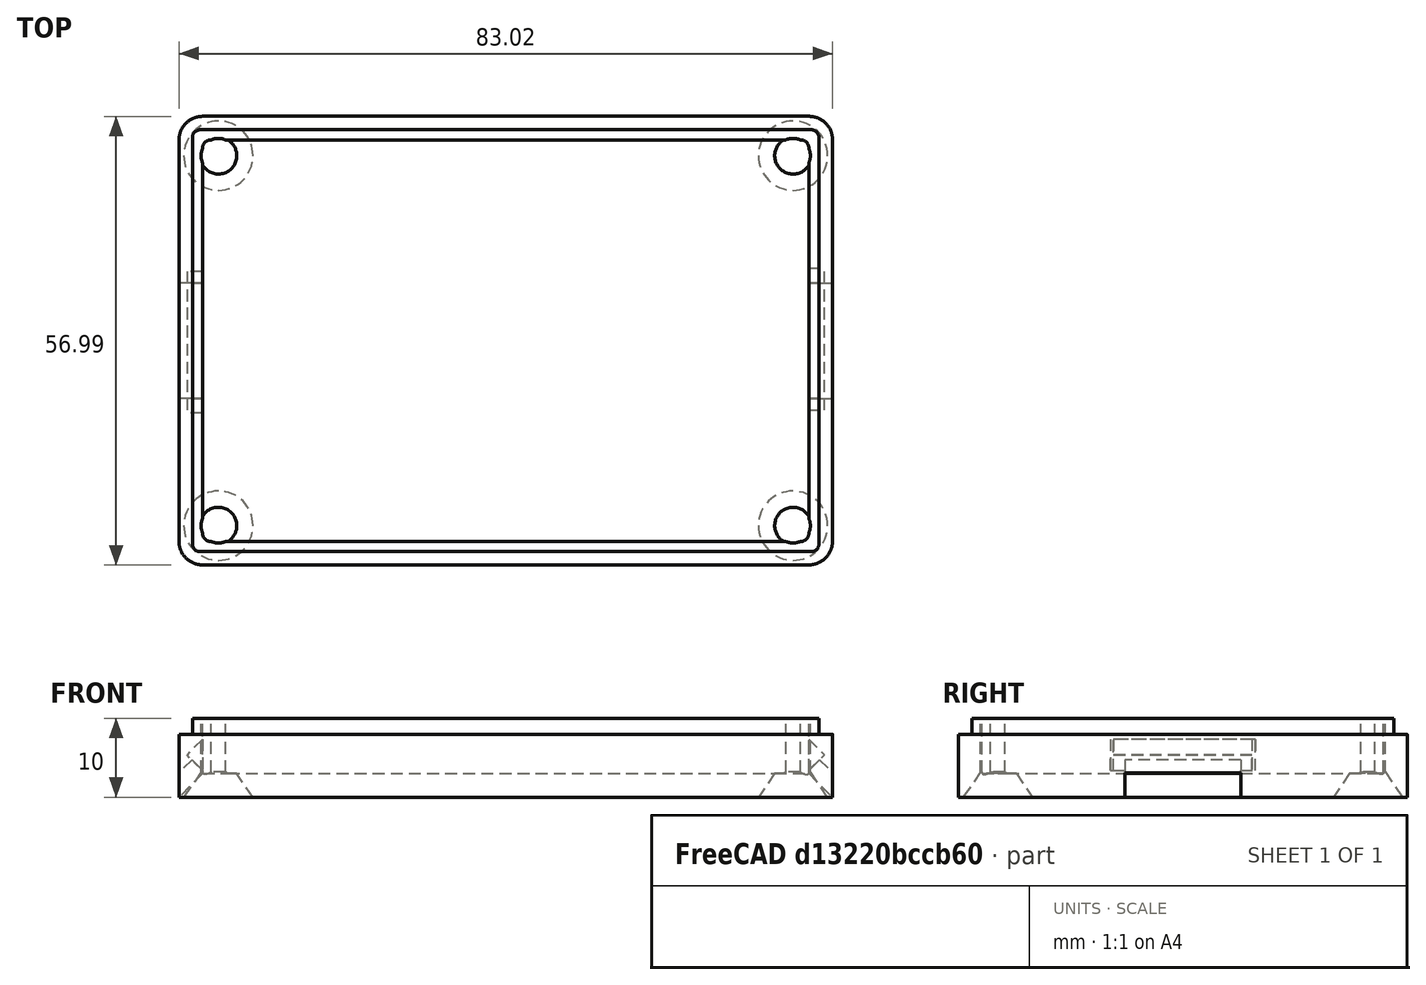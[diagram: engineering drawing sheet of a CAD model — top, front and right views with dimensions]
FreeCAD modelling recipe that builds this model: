
FCSTD DOCUMENT  (FreeCAD 0.18.4R)
Label: MidBoxBottom
License: All rights reserved
LicenseURL: http://en.wikipedia.org/wiki/All_rights_reserved
objects: Part::Box×11, Part::MultiFuse×8, Part::Cut×5, Part::Cylinder×4, Part::Cone×4, Part::Fillet×2, Sketcher::SketchObject×1, PartDesign::Pad×1, Mesh::Feature×1
note: 37 computed .brp shape members not serialized (recipe doc carries the construction recipe); baked Part::Feature solids carry a one-line shape summary decoded from their .brp

FEATURE [Sketcher::SketchObject] Sketch002
  MapMode = 5
  sketch-geometry (8):
    g0: LineSegment StartX=6.98534 StartY=-27.9862 StartZ=0 EndX=-70.0102 EndY=-27.9862 EndZ=0
    g1: LineSegment StartX=-73.0017 StartY=-24.9946 StartZ=0 EndX=-73.0017 EndY=25.9928 EndZ=0
    g2: LineSegment StartX=-69.9918 StartY=29.0027 StartZ=0 EndX=7.02245 EndY=29.0027 EndZ=0
    g3: LineSegment StartX=10.0166 StartY=26.0085 StartZ=0 EndX=10.0166 EndY=-24.9549 EndZ=0
    g4: ArcOfCircle CenterX=6.98534 CenterY=-24.9549 CenterZ=0 NormalX=0 NormalY=0 NormalZ=1 AngleXU=0 Radius=3.0313 StartAngle=4.71239 EndAngle=6.28319
    g5: ArcOfCircle CenterX=-70.0102 CenterY=-24.9946 CenterZ=0 NormalX=0 NormalY=0 NormalZ=1 AngleXU=0 Radius=2.99151 StartAngle=3.14159 EndAngle=4.71239
    g6: ArcOfCircle CenterX=-69.9918 CenterY=25.9928 CenterZ=0 NormalX=0 NormalY=0 NormalZ=1 AngleXU=0 Radius=3.00989 StartAngle=1.5708 EndAngle=3.14159
    g7: ArcOfCircle CenterX=7.02245 CenterY=26.0085 CenterZ=0 NormalX=0 NormalY=0 NormalZ=1 AngleXU=0 Radius=2.99419 StartAngle=1.03e-13 EndAngle=1.5708
  constraints (12):
    c: Horizontal(g0)
    c: Horizontal(g2)
    c: Vertical(g1)
    c: Vertical(g3)
    c: Tangent(g3,g4) = 1.5708
    c: Tangent(g0,g4) = 1.5708
    c: Tangent(g1,g5) = 1.5708
    c: Tangent(g0,g5) = 1.5708
    c: Tangent(g1,g6) = 1.5708
    c: Tangent(g2,g6) = 1.5708
    c: Tangent(g2,g7) = 1.5708
    c: Tangent(g3,g7) = 1.5708
FEATURE [PartDesign::Pad] Pad013
  Length = 10
  Length2 = 100
  Profile = -> Sketch002
  Type = 0
FEATURE [Part::Box] Box010  label="Würfel010"
  AttacherType = Attacher::AttachEngine3D
  Height = 9
  Length = 77
  Placement = pos=(-70,-25,3) rot=(0,0,1;0rad)
  Width = 51
FEATURE [Part::Cut] Cut011  label="Box raw"
  Base = -> Pad013
  Tool = -> Box010
FEATURE [Part::Box] Box  label="Rand002"
  AttacherType = Attacher::AttachEngine3D
  Height = 2
  Length = 83
  Placement = pos=(-73,27.3,14) rot=(0,0,1;0rad)
  Width = 2
FEATURE [Part::Box] Box011  label="Rand001"
  AttacherType = Attacher::AttachEngine3D
  Height = 2
  Length = 83
  Placement = pos=(-73,-28.3,14) rot=(0,0,1;0rad)
  Width = 2
FEATURE [Part::Box] Box012  label="Rand003"
  AttacherType = Attacher::AttachEngine3D
  Height = 2
  Length = 2
  Placement = pos=(-73.3,-28,14) rot=(0,0,1;0rad)
  Width = 57
FEATURE [Part::Box] Box013  label="Rand004"
  AttacherType = Attacher::AttachEngine3D
  Height = 2
  Length = 2
  Placement = pos=(8.3,-28,14) rot=(0,0,1;0rad)
  Width = 57
FEATURE [Part::Cylinder] Cylinder005  label="Zylinder"
  Angle = 360
  AttacherType = Attacher::AttachEngine3D
  Height = 18
  Placement = pos=(12,-23,-1) rot=(0,0,1;0rad)
  Radius = 2.2
FEATURE [Part::Cone] Cone  label="Kegel"
  Angle = 360
  AttacherType = Attacher::AttachEngine3D
  Height = 3.2
  Placement = pos=(12,-23,-1) rot=(0,0,1;0rad)
  Radius1 = 4.4
  Radius2 = 2.2
FEATURE [Part::MultiFuse] Fusion002  label="Bohrung001"
  Placement = pos=(-7,0,1) rot=(0,0,1;0rad)
  Shapes = -> [Cylinder005,Cone]
FEATURE [Part::Cylinder] Cylinder006  label="Zylinder003"
  Angle = 360
  AttacherType = Attacher::AttachEngine3D
  Height = 18
  Placement = pos=(12,-23,-1) rot=(0,0,1;0rad)
  Radius = 2.2
FEATURE [Part::Cone] Cone001  label="Kegel001"
  Angle = 360
  AttacherType = Attacher::AttachEngine3D
  Height = 3.2
  Placement = pos=(12,-23,-1) rot=(0,0,1;0rad)
  Radius1 = 4.4
  Radius2 = 2.2
FEATURE [Part::MultiFuse] Fusion003  label="Bohrung002"
  Placement = pos=(-7,47,1) rot=(0,0,1;0rad)
  Shapes = -> [Cylinder006,Cone001]
FEATURE [Part::Cylinder] Cylinder007  label="Zylinder004"
  Angle = 360
  AttacherType = Attacher::AttachEngine3D
  Height = 18
  Placement = pos=(12,-23,-1) rot=(0,0,1;0rad)
  Radius = 2.2
FEATURE [Part::Cone] Cone002  label="Kegel002"
  Angle = 360
  AttacherType = Attacher::AttachEngine3D
  Height = 3.2
  Placement = pos=(12,-23,-1) rot=(0,0,1;0rad)
  Radius1 = 4.4
  Radius2 = 2.2
FEATURE [Part::MultiFuse] Fusion004  label="Bohrung003"
  Placement = pos=(-80,0,1) rot=(0,0,1;0rad)
  Shapes = -> [Cylinder007,Cone002]
FEATURE [Part::Cylinder] Cylinder008  label="Zylinder005"
  Angle = 360
  AttacherType = Attacher::AttachEngine3D
  Height = 18
  Placement = pos=(12,-23,-1) rot=(0,0,1;0rad)
  Radius = 2.2
FEATURE [Part::Cone] Cone003  label="Kegel003"
  Angle = 360
  AttacherType = Attacher::AttachEngine3D
  Height = 3.2
  Placement = pos=(12,-23,-1) rot=(0,0,1;0rad)
  Radius1 = 4.4
  Radius2 = 2.2
FEATURE [Part::MultiFuse] Fusion005  label="Bohrung004"
  Placement = pos=(-80,47,1) rot=(0,0,1;0rad)
  Shapes = -> [Cylinder008,Cone003]
FEATURE [Part::MultiFuse] Fusion  label="RandFraesung"
  Placement = pos=(0,0,-6) rot=(0,0,1;0rad)
  Shapes = -> [Box013,Box011,Box012,Box]
FEATURE [Part::Cut] Cut
  Base = -> Cut011
  Tool = -> Fusion
FEATURE [Part::Box] Box020  label="Kabeltunnel"
  AttacherType = Attacher::AttachEngine3D
  Height = 2.2
  Length = 10
  Placement = pos=(12,-6.85,5.5) rot=(0,1,0;0.785398rad)
  Width = 14.7
FEATURE [Part::Box] Box021  label="KabelTunnelDichtungsSchacht"
  AttacherType = Attacher::AttachEngine3D
  Height = 4
  Length = 8
  Placement = pos=(8,-8.3,8.2) rot=(0,1,0;0.785398rad)
  Width = 18
FEATURE [Part::Box] Box022  label="Kabeltunnel003"
  AttacherType = Attacher::AttachEngine3D
  Height = 2.2
  Length = 10
  Placement = pos=(12,-6.85,5.5) rot=(0,1,0;0.785398rad)
  Width = 14.7
FEATURE [Part::Box] Box023  label="KabelTunnelDichtungsSchacht001"
  AttacherType = Attacher::AttachEngine3D
  Height = 4
  Length = 8
  Placement = pos=(8,-8.3,8.2) rot=(0,1,0;0.785398rad)
  Width = 18
FEATURE [Part::MultiFuse] Fusion007  label="Kabelschacht001"
  Placement = pos=(-7.5,0,0) rot=(0,0,1;0rad)
  Shapes = -> [Box020,Box021]
FEATURE [Part::MultiFuse] Fusion008  label="Kabelschacht002"
  Placement = pos=(-55.5,1,0) rot=(0,0,1;3.14159rad)
  Shapes = -> [Box022,Box023]
FEATURE [Part::Box] Box024  label="Würfel"
  AttacherType = Attacher::AttachEngine3D
  Height = 3.2
  Length = 10
  Placement = pos=(-3.2,-9,0) rot=(0,0,1;0rad)
  Width = 20
FEATURE [Part::Cut] Cut012
  Base = -> Fusion007
  Tool = -> Box024
FEATURE [Part::Box] Box025  label="Würfel011"
  AttacherType = Attacher::AttachEngine3D
  Height = 3.2
  Length = 10
  Placement = pos=(-69.8,-9,0) rot=(0,0,1;0rad)
  Width = 20
FEATURE [Part::Cut] Cut013
  Base = -> Fusion008
  Tool = -> Box025
FEATURE [Part::MultiFuse] Fusion009  label="Bohrungen"
  Shapes = -> [Fusion003,Cut013,Fusion004,Fusion005,Fusion002,Cut012]
FEATURE [Part::Cut] Cut014
  Base = -> Cut
  Tool = -> Fusion009
FEATURE [Part::Fillet] Fillet
  Base = -> Cut014
  Edges = 4 edges r=1: [Edge130,Edge131,Edge205,Edge206]
FEATURE [Part::Fillet] Fillet001
  Base = -> Fillet
  Edges = 4 edges r=1: [Edge117,Edge127,Edge151,Edge166]
FEATURE [Mesh::Feature] Mesh  label="Fillet001 (Meshed)"
